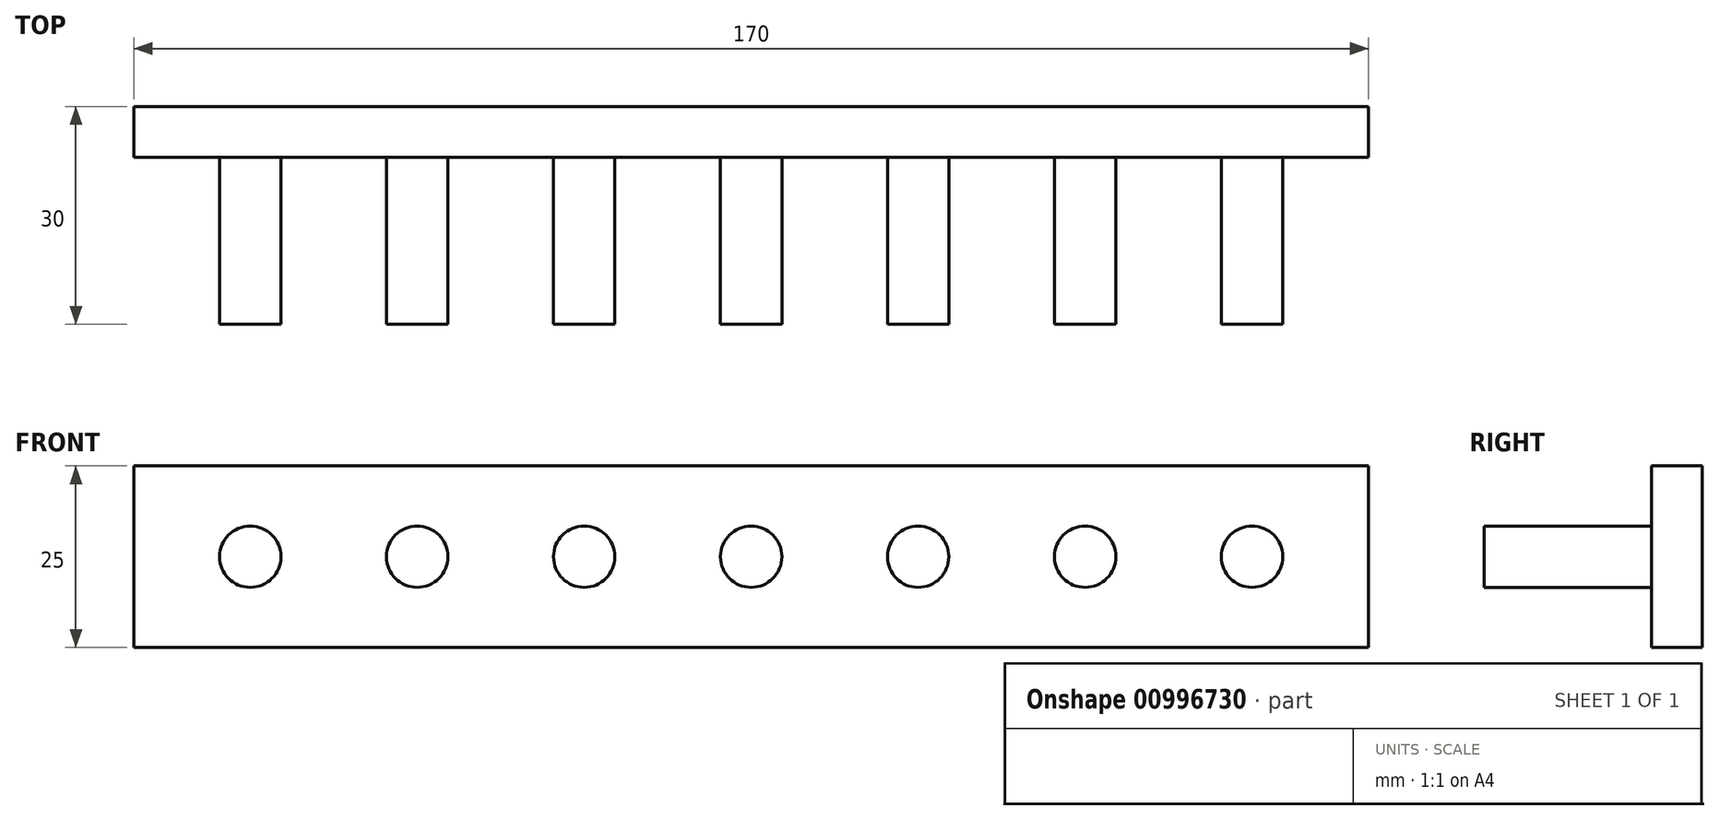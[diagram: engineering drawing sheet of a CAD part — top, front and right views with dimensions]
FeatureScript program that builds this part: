
annotation { "Feature Type Name" : "Feature", "Feature Type Description" : "" }
export const myFeature = defineFeature(function(context is Context, id is Id, definition is map)
    precondition{}
    {
        {
            var Q0;
            Q0=qCreatedBy(makeId("Front.planeOp"),FACE);
            var sketch = newSketch(context, id + "F0", { "sketchPlane" : qUnion([Q0])});
            skLineSegment(sketch, "E0.bottom", {"start": v(0, 0) * mm, "end": v(170, 0) * mm});
            skLineSegment(sketch, "E0.top", {"start": v(0, -25) * mm, "end": v(170, -25) * mm});
            skLineSegment(sketch, "E0.left", {"start": v(0, 0) * mm, "end": v(0, -25) * mm});
            skLineSegment(sketch, "E0.right", {"start": v(170, 0) * mm, "end": v(170, -25) * mm});
            skSolve(sketch);
        }
        {
            var Q0;
            Q0 = qSketchRegion(id + "F0", true);
            extrude(context, id + "F1", {"entities" : qUnion([Q0]), "depth" : 7 * mm, "offsetDistance" : 25 * mm});
        }
        {
            var Q0;
            Q0=makeQuery(id+"F1.opExtrude","CAP_FACE",FACE,{"disambiguationData":[OSD([sQuery(id+"F0.wireOp",EDGE,"E0.bottom"),sQuery(id+"F0.wireOp",EDGE,"E0.top"),sQuery(id+"F0.wireOp",EDGE,"E0.left"),sQuery(id+"F0.wireOp",EDGE,"E0.right")])],"isStart":false});
            var sketch = newSketch(context, id + "F2", { "sketchPlane" : qUnion([Q0])});
            skLineSegment(sketch, "E1", {"start": v(0, -12.5) * mm, "end": v(170, -12.5) * mm, "construction": true});
            skCircle(sketch, "E2", {"center": v(85, -12.5) * mm, "radius": 4.23 * mm});
            skCircle(sketch, "E3.1.0.0", {"center": v(108, -12.5) * mm, "radius": 4.23 * mm});
            skCircle(sketch, "E3.2.0.0", {"center": v(131, -12.5) * mm, "radius": 4.23 * mm});
            skCircle(sketch, "E3.3.0.0", {"center": v(154, -12.5) * mm, "radius": 4.23 * mm});
            skLineSegment(sketch, "E3.direction1", {"start": v(85, -12.5) * mm, "end": v(108, -12.5) * mm, "construction": true});
            skCircle(sketch, "E4.1.0.0", {"center": v(62, -12.5) * mm, "radius": 4.23 * mm});
            skCircle(sketch, "E4.2.0.0", {"center": v(39, -12.5) * mm, "radius": 4.23 * mm});
            skCircle(sketch, "E4.3.0.0", {"center": v(16, -12.5) * mm, "radius": 4.23 * mm});
            skLineSegment(sketch, "E4.direction1", {"start": v(85, -12.5) * mm, "end": v(62, -12.5) * mm, "construction": true});
            skSolve(sketch);
        }
        {
            var Q0;
            Q0 = qSketchRegion(id + "F2", true);
            extrude(context, id + "F3", {"entities" : qUnion([Q0]), "operationType" : NewBodyOperationType.ADD, "depth" : 23 * mm, "offsetDistance" : 25 * mm});
        }
    });
